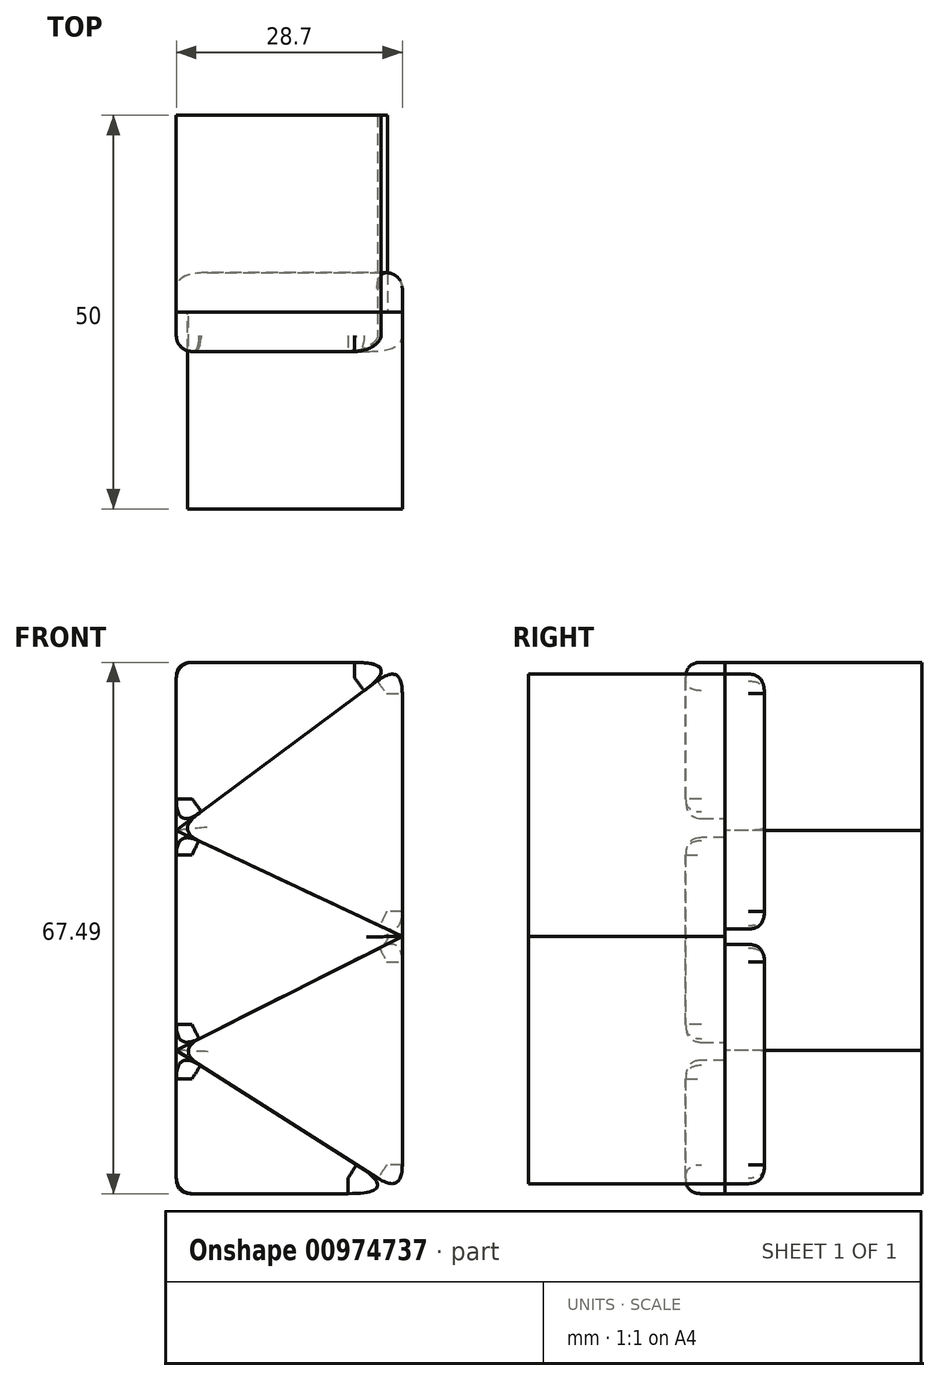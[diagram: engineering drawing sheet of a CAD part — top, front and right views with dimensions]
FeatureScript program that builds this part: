
annotation { "Feature Type Name" : "Feature", "Feature Type Description" : "" }
export const myFeature = defineFeature(function(context is Context, id is Id, definition is map)
    precondition{}
    {
        {
            var Q0;
            Q0=qCreatedBy(makeId("Front.planeOp"),FACE);
            var sketch = newSketch(context, id + "F0", { "sketchPlane" : qUnion([Q0])});
            skLineSegment(sketch, "E0.bottom", {"start": v(-14.25, 34.81) * mm, "end": v(14.45, 34.81) * mm});
            skLineSegment(sketch, "E0.top", {"start": v(-14.25, -32.68) * mm, "end": v(14.45, -32.68) * mm});
            skLineSegment(sketch, "E0.left", {"start": v(-14.25, 34.81) * mm, "end": v(-14.25, -32.68) * mm});
            skLineSegment(sketch, "E0.right", {"start": v(14.45, 34.81) * mm, "end": v(14.45, -32.68) * mm});
            skLineSegment(sketch, "E1", {"start": v(-14.25, 13.48) * mm, "end": v(14.45, 34.81) * mm});
            skLineSegment(sketch, "E2", {"start": v(-14.25, 13.48) * mm, "end": v(14.45, 0) * mm});
            skLineSegment(sketch, "E3", {"start": v(14.45, 0) * mm, "end": v(-14.25, -14.45) * mm});
            skLineSegment(sketch, "E4", {"start": v(-14.25, -14.45) * mm, "end": v(14.45, -32.68) * mm});
            skSolve(sketch);
        }
        {
            var Q0;
            {var subQ0=sQuery(id+"F0.wireOp",EDGE,"E1");Q0=makeQuery(id+"F0.imprint","IMPRINT",FACE,{"disambiguationData":[TD([[makeQuery(id+"F0.imprint","IMPRINT",EDGE,{"derivedFrom":subQ0}),-1.0]])]});}
            var Q1;
            {var subQ2=sQuery(id+"F0.wireOp",EDGE,"E3");Q1=makeQuery(id+"F0.imprint","IMPRINT",FACE,{"disambiguationData":[TD([[makeQuery(id+"F0.imprint","IMPRINT",EDGE,{"derivedFrom":subQ2}),1.0]])]});}
            extrude(context, id + "F1", {"entities" : qUnion([Q0, Q1]), "depth" : 25 * mm, "offsetDistance" : 25 * mm});
        }
        {
            var Q0;
            {var subQ0=sQuery(id+"F0.wireOp",EDGE,"E2");Q0=makeQuery(id+"F0.imprint","IMPRINT",FACE,{"disambiguationData":[TD([[makeQuery(id+"F0.imprint","IMPRINT",EDGE,{"derivedFrom":subQ0}),-1.0]])]});}
            var Q1;
            {var subQ0=sQuery(id+"F0.wireOp",EDGE,"E0.bottom");Q1=makeQuery(id+"F0.imprint","IMPRINT",FACE,{"disambiguationData":[TD([[makeQuery(id+"F0.imprint","IMPRINT",EDGE,{"derivedFrom":subQ0}),-1.0]])]});}
            var Q2;
            {var subQ0=sQuery(id+"F0.wireOp",EDGE,"E0.top");Q2=makeQuery(id+"F0.imprint","IMPRINT",FACE,{"disambiguationData":[TD([[makeQuery(id+"F0.imprint","IMPRINT",EDGE,{"derivedFrom":subQ0}),1.0]])]});}
            extrude(context, id + "F2", {"entities" : qUnion([Q0, Q1, Q2]), "oppositeDirection" : true, "depth" : 25 * mm, "offsetDistance" : 25 * mm});
        }
        {
            var Q0;
            {var subQ0=sQuery(id+"F0.wireOp",EDGE,"E1");Q0=makeQuery(id+"F0.imprint","IMPRINT",FACE,{"disambiguationData":[TD([[makeQuery(id+"F0.imprint","IMPRINT",EDGE,{"derivedFrom":subQ0}),-1.0]])]});}
            var Q1;
            {var subQ2=sQuery(id+"F0.wireOp",EDGE,"E3");Q1=makeQuery(id+"F0.imprint","IMPRINT",FACE,{"disambiguationData":[TD([[makeQuery(id+"F0.imprint","IMPRINT",EDGE,{"derivedFrom":subQ2}),1.0]])]});}
            extrude(context, id + "F3", {"entities" : qUnion([Q0, Q1]), "oppositeDirection" : true, "depth" : 5 * mm, "offsetDistance" : 25 * mm});
        }
        {
            var Q0;
            {var subQ0=sQuery(id+"F0.wireOp",EDGE,"E0.bottom");Q0=makeQuery(id+"F0.imprint","IMPRINT",FACE,{"disambiguationData":[TD([[makeQuery(id+"F0.imprint","IMPRINT",EDGE,{"derivedFrom":subQ0}),-1.0]])]});}
            var Q1;
            {var subQ0=sQuery(id+"F0.wireOp",EDGE,"E2");Q1=makeQuery(id+"F0.imprint","IMPRINT",FACE,{"disambiguationData":[TD([[makeQuery(id+"F0.imprint","IMPRINT",EDGE,{"derivedFrom":subQ0}),-1.0]])]});}
            var Q2;
            {var subQ0=sQuery(id+"F0.wireOp",EDGE,"E0.top");Q2=makeQuery(id+"F0.imprint","IMPRINT",FACE,{"disambiguationData":[TD([[makeQuery(id+"F0.imprint","IMPRINT",EDGE,{"derivedFrom":subQ0}),1.0]])]});}
            extrude(context, id + "F4", {"entities" : qUnion([Q0, Q1, Q2]), "depth" : 5 * mm, "offsetDistance" : 25 * mm});
        }
        {
            var Q0;
            {var subQ0=sQuery(id+"F0.wireOp",EDGE,"E0.left");Q0=makeQuery(id+"F4.opExtrude","CAP_EDGE",EDGE,{"disambiguationData":[OSD([subQ0]),TDD([makeQuery(id+"F0.imprint","IMPRINT",EDGE,{"disambiguationData":[TD([[makeQuery(id+"F0.imprint","INTERSECT",VERTEX,{"derivedFrom":[sQuery(id+"F0.wireOp",EDGE,"E0.bottom"),subQ0]}),-1.0]])],"derivedFrom":subQ0})])],"isStart":false});}
            var Q1;
            {var subQ0=sQuery(id+"F0.wireOp",EDGE,"E0.left");Q1=makeQuery(id+"F4.opExtrude","CAP_EDGE",EDGE,{"disambiguationData":[OSD([subQ0]),TDD([makeQuery(id+"F0.imprint","IMPRINT",EDGE,{"disambiguationData":[TD([[makeQuery(id+"F0.imprint","INTERSECT",VERTEX,{"derivedFrom":[subQ0,sQuery(id+"F0.wireOp",EDGE,"E1"),sQuery(id+"F0.wireOp",EDGE,"E2")]}),-1.0]])],"derivedFrom":subQ0})])],"isStart":false});}
            var Q2;
            {var subQ0=sQuery(id+"F0.wireOp",EDGE,"E0.left");Q2=makeQuery(id+"F4.opExtrude","CAP_EDGE",EDGE,{"disambiguationData":[OSD([subQ0]),TDD([makeQuery(id+"F0.imprint","IMPRINT",EDGE,{"disambiguationData":[TD([[makeQuery(id+"F0.imprint","INTERSECT",VERTEX,{"derivedFrom":[sQuery(id+"F0.wireOp",EDGE,"E0.top"),subQ0]}),1.0]])],"derivedFrom":subQ0})])],"isStart":false});}
            var Q3;
            {var subQ0=sQuery(id+"F0.wireOp",EDGE,"E0.right");Q3=makeQuery(id+"F3.opExtrude","CAP_EDGE",EDGE,{"disambiguationData":[OSD([subQ0]),TDD([makeQuery(id+"F0.imprint","IMPRINT",EDGE,{"disambiguationData":[TD([[makeQuery(id+"F0.imprint","INTERSECT",VERTEX,{"derivedFrom":[sQuery(id+"F0.wireOp",EDGE,"E0.bottom"),subQ0,sQuery(id+"F0.wireOp",EDGE,"E1")]}),-1.0]])],"derivedFrom":subQ0})])],"isStart":false});}
            var Q4;
            {var subQ0=sQuery(id+"F0.wireOp",EDGE,"E0.right");Q4=makeQuery(id+"F3.opExtrude","CAP_EDGE",EDGE,{"disambiguationData":[OSD([subQ0]),TDD([makeQuery(id+"F0.imprint","IMPRINT",EDGE,{"disambiguationData":[TD([[makeQuery(id+"F0.imprint","INTERSECT",VERTEX,{"derivedFrom":[sQuery(id+"F0.wireOp",EDGE,"E0.top"),subQ0,sQuery(id+"F0.wireOp",EDGE,"E4")]}),1.0]])],"derivedFrom":subQ0})])],"isStart":false});}
            fillet(context, id + "F5", {"entities" : qUnion([Q0, Q1, Q2, Q3, Q4]), "radius" : 2 * mm, "tangentPropagation" : true, "allowEdgeOverflow" : false});
        }
        {
            var Q0;
            Q0=makeQuery(id+"F2.opExtrude","SWEPT_EDGE",EDGE,{"disambiguationData":[OSD([sQuery(id+"F0.wireOp",EDGE,"E0.bottom"),sQuery(id+"F0.wireOp",EDGE,"E0.right"),sQuery(id+"F0.wireOp",EDGE,"E1")])]});
            var Q1;
            Q1=makeQuery(id+"F2.opExtrude","SWEPT_EDGE",EDGE,{"disambiguationData":[OSD([sQuery(id+"F0.wireOp",EDGE,"E0.right"),sQuery(id+"F0.wireOp",EDGE,"E2"),sQuery(id+"F0.wireOp",EDGE,"E3")])]});
            var Q2;
            Q2=makeQuery(id+"F2.opExtrude","SWEPT_EDGE",EDGE,{"disambiguationData":[OSD([sQuery(id+"F0.wireOp",EDGE,"E0.top"),sQuery(id+"F0.wireOp",EDGE,"E0.right"),sQuery(id+"F0.wireOp",EDGE,"E4")])]});
            fillet(context, id + "F6", {"entities" : qUnion([Q0, Q1, Q2]), "radius" : 2 * mm, "tangentPropagation" : true, "rho" : 0.5, "crossSection" : FilletCrossSection.CONIC, "allowEdgeOverflow" : false});
        }
        {
            var Q0;
            Q0=makeQuery(id+"F1.opExtrude","SWEPT_EDGE",EDGE,{"disambiguationData":[OSD([sQuery(id+"F0.wireOp",EDGE,"E0.left"),sQuery(id+"F0.wireOp",EDGE,"E1"),sQuery(id+"F0.wireOp",EDGE,"E2")])]});
            var Q1;
            Q1=makeQuery(id+"F1.opExtrude","SWEPT_EDGE",EDGE,{"disambiguationData":[OSD([sQuery(id+"F0.wireOp",EDGE,"E0.left"),sQuery(id+"F0.wireOp",EDGE,"E3"),sQuery(id+"F0.wireOp",EDGE,"E4")])]});
            fillet(context, id + "F7", {"entities" : qUnion([Q0, Q1]), "radius" : 2 * mm, "tangentPropagation" : true, "rho" : 0.5, "crossSection" : FilletCrossSection.CONIC, "allowEdgeOverflow" : false});
        }
        {
            var Q0;
            {var subQ0=sQuery(id+"F0.wireOp",EDGE,"E1");var subQ1=sQuery(id+"F0.wireOp",EDGE,"E0.right");Q0=makeQuery(id+"F5.opFillet","BLEND_EDGE",EDGE,{"blendedFrom":[makeQuery(id+"F3.opExtrude","CAP_EDGE",EDGE,{"disambiguationData":[OSD([subQ1]),TDD([makeQuery(id+"F0.imprint","IMPRINT",EDGE,{"disambiguationData":[TD([[makeQuery(id+"F0.imprint","INTERSECT",VERTEX,{"derivedFrom":[sQuery(id+"F0.wireOp",EDGE,"E0.bottom"),subQ1,subQ0]}),-1.0]])],"derivedFrom":subQ1})])],"isStart":false}),makeQuery(id+"F3.opExtrude","SWEPT_FACE",FACE,{"disambiguationData":[OSD([subQ0])]})],"blendedInto":[makeQuery(id+"F3.opExtrude","SWEPT_FACE",FACE,{"disambiguationData":[OSD([subQ0])]})]});}
            var Q1;
            {var subQ0=sQuery(id+"F0.wireOp",EDGE,"E4");var subQ1=sQuery(id+"F0.wireOp",EDGE,"E0.right");Q1=makeQuery(id+"F5.opFillet","BLEND_EDGE",EDGE,{"blendedFrom":[makeQuery(id+"F3.opExtrude","CAP_EDGE",EDGE,{"disambiguationData":[OSD([subQ1]),TDD([makeQuery(id+"F0.imprint","IMPRINT",EDGE,{"disambiguationData":[TD([[makeQuery(id+"F0.imprint","INTERSECT",VERTEX,{"derivedFrom":[sQuery(id+"F0.wireOp",EDGE,"E0.top"),subQ1,subQ0]}),1.0]])],"derivedFrom":subQ1})])],"isStart":false}),makeQuery(id+"F3.opExtrude","SWEPT_FACE",FACE,{"disambiguationData":[OSD([subQ0])]})],"blendedInto":[makeQuery(id+"F3.opExtrude","SWEPT_FACE",FACE,{"disambiguationData":[OSD([subQ0])]})]});}
            var Q2;
            {var subQ0=sQuery(id+"F0.wireOp",EDGE,"E2");var subQ1=sQuery(id+"F0.wireOp",EDGE,"E0.left");Q2=makeQuery(id+"F5.opFillet","BLEND_EDGE",EDGE,{"blendedFrom":[makeQuery(id+"F4.opExtrude","CAP_EDGE",EDGE,{"disambiguationData":[OSD([subQ1]),TDD([makeQuery(id+"F0.imprint","IMPRINT",EDGE,{"disambiguationData":[TD([[makeQuery(id+"F0.imprint","INTERSECT",VERTEX,{"derivedFrom":[subQ1,sQuery(id+"F0.wireOp",EDGE,"E1"),subQ0]}),-1.0]])],"derivedFrom":subQ1})])],"isStart":false}),makeQuery(id+"F4.opExtrude","SWEPT_FACE",FACE,{"disambiguationData":[OSD([subQ0])]})],"blendedInto":[makeQuery(id+"F4.opExtrude","SWEPT_FACE",FACE,{"disambiguationData":[OSD([subQ0])]})]});}
            var Q3;
            {var subQ0=sQuery(id+"F0.wireOp",EDGE,"E1");var subQ1=sQuery(id+"F0.wireOp",EDGE,"E0.left");Q3=makeQuery(id+"F5.opFillet","BLEND_EDGE",EDGE,{"blendedFrom":[makeQuery(id+"F4.opExtrude","CAP_EDGE",EDGE,{"disambiguationData":[OSD([subQ1]),TDD([makeQuery(id+"F0.imprint","IMPRINT",EDGE,{"disambiguationData":[TD([[makeQuery(id+"F0.imprint","INTERSECT",VERTEX,{"derivedFrom":[sQuery(id+"F0.wireOp",EDGE,"E0.bottom"),subQ1]}),-1.0]])],"derivedFrom":subQ1})])],"isStart":false}),makeQuery(id+"F4.opExtrude","SWEPT_FACE",FACE,{"disambiguationData":[OSD([subQ0])]})],"blendedInto":[makeQuery(id+"F4.opExtrude","SWEPT_FACE",FACE,{"disambiguationData":[OSD([subQ0])]})]});}
            var Q4;
            {var subQ0=sQuery(id+"F0.wireOp",EDGE,"E3");var subQ1=sQuery(id+"F0.wireOp",EDGE,"E0.left");Q4=makeQuery(id+"F5.opFillet","BLEND_EDGE",EDGE,{"blendedFrom":[makeQuery(id+"F4.opExtrude","CAP_EDGE",EDGE,{"disambiguationData":[OSD([subQ1]),TDD([makeQuery(id+"F0.imprint","IMPRINT",EDGE,{"disambiguationData":[TD([[makeQuery(id+"F0.imprint","INTERSECT",VERTEX,{"derivedFrom":[subQ1,sQuery(id+"F0.wireOp",EDGE,"E1"),sQuery(id+"F0.wireOp",EDGE,"E2")]}),-1.0]])],"derivedFrom":subQ1})])],"isStart":false}),makeQuery(id+"F4.opExtrude","SWEPT_FACE",FACE,{"disambiguationData":[OSD([subQ0])]})],"blendedInto":[makeQuery(id+"F4.opExtrude","SWEPT_FACE",FACE,{"disambiguationData":[OSD([subQ0])]})]});}
            var Q5;
            {var subQ0=sQuery(id+"F0.wireOp",EDGE,"E4");var subQ1=sQuery(id+"F0.wireOp",EDGE,"E0.left");Q5=makeQuery(id+"F5.opFillet","BLEND_EDGE",EDGE,{"blendedFrom":[makeQuery(id+"F4.opExtrude","CAP_EDGE",EDGE,{"disambiguationData":[OSD([subQ1]),TDD([makeQuery(id+"F0.imprint","IMPRINT",EDGE,{"disambiguationData":[TD([[makeQuery(id+"F0.imprint","INTERSECT",VERTEX,{"derivedFrom":[sQuery(id+"F0.wireOp",EDGE,"E0.top"),subQ1]}),1.0]])],"derivedFrom":subQ1})])],"isStart":false}),makeQuery(id+"F4.opExtrude","SWEPT_FACE",FACE,{"disambiguationData":[OSD([subQ0])]})],"blendedInto":[makeQuery(id+"F4.opExtrude","SWEPT_FACE",FACE,{"disambiguationData":[OSD([subQ0])]})]});}
            var Q6;
            {var subQ0=sQuery(id+"F0.wireOp",EDGE,"E3");var subQ1=sQuery(id+"F0.wireOp",EDGE,"E0.right");Q6=makeQuery(id+"F5.opFillet","BLEND_EDGE",EDGE,{"blendedFrom":[makeQuery(id+"F3.opExtrude","CAP_EDGE",EDGE,{"disambiguationData":[OSD([subQ1]),TDD([makeQuery(id+"F0.imprint","IMPRINT",EDGE,{"disambiguationData":[TD([[makeQuery(id+"F0.imprint","INTERSECT",VERTEX,{"derivedFrom":[sQuery(id+"F0.wireOp",EDGE,"E0.top"),subQ1,sQuery(id+"F0.wireOp",EDGE,"E4")]}),1.0]])],"derivedFrom":subQ1})])],"isStart":false}),makeQuery(id+"F3.opExtrude","SWEPT_FACE",FACE,{"disambiguationData":[OSD([subQ0])]})],"blendedInto":[makeQuery(id+"F3.opExtrude","SWEPT_FACE",FACE,{"disambiguationData":[OSD([subQ0])]})]});}
            var Q7;
            {var subQ0=sQuery(id+"F0.wireOp",EDGE,"E2");var subQ1=sQuery(id+"F0.wireOp",EDGE,"E0.right");Q7=makeQuery(id+"F5.opFillet","BLEND_EDGE",EDGE,{"blendedFrom":[makeQuery(id+"F3.opExtrude","CAP_EDGE",EDGE,{"disambiguationData":[OSD([subQ1]),TDD([makeQuery(id+"F0.imprint","IMPRINT",EDGE,{"disambiguationData":[TD([[makeQuery(id+"F0.imprint","INTERSECT",VERTEX,{"derivedFrom":[sQuery(id+"F0.wireOp",EDGE,"E0.bottom"),subQ1,sQuery(id+"F0.wireOp",EDGE,"E1")]}),-1.0]])],"derivedFrom":subQ1})])],"isStart":false}),makeQuery(id+"F3.opExtrude","SWEPT_FACE",FACE,{"disambiguationData":[OSD([subQ0])]})],"blendedInto":[makeQuery(id+"F3.opExtrude","SWEPT_FACE",FACE,{"disambiguationData":[OSD([subQ0])]})]});}
            fillet(context, id + "F8", {"entities" : qUnion([Q0, Q1, Q2, Q3, Q4, Q5, Q6, Q7]), "radius" : 2 * mm, "tangentPropagation" : true, "rho" : 0.5, "crossSection" : FilletCrossSection.CONIC, "allowEdgeOverflow" : false});
        }
        {
            var Q0;
            Q0=makeQuery(id+"F8.opFillet","BLEND_EDGE",EDGE,{"blendedFrom":[makeQuery(id+"F4.opExtrude","CAP_EDGE",EDGE,{"disambiguationData":[OSD([sQuery(id+"F0.wireOp",EDGE,"E1")])],"isStart":false}),makeQuery(id+"F4.opExtrude","SWEPT_FACE",FACE,{"disambiguationData":[OSD([sQuery(id+"F0.wireOp",EDGE,"E0.bottom")])]})],"blendedInto":[makeQuery(id+"F4.opExtrude","SWEPT_FACE",FACE,{"disambiguationData":[OSD([sQuery(id+"F0.wireOp",EDGE,"E0.bottom")])]})]});
            var Q1;
            Q1=makeQuery(id+"F8.opFillet","BLEND_EDGE",EDGE,{"blendedFrom":[makeQuery(id+"F4.opExtrude","CAP_EDGE",EDGE,{"disambiguationData":[OSD([sQuery(id+"F0.wireOp",EDGE,"E4")])],"isStart":false}),makeQuery(id+"F4.opExtrude","SWEPT_FACE",FACE,{"disambiguationData":[OSD([sQuery(id+"F0.wireOp",EDGE,"E0.top")])]})],"blendedInto":[makeQuery(id+"F4.opExtrude","SWEPT_FACE",FACE,{"disambiguationData":[OSD([sQuery(id+"F0.wireOp",EDGE,"E0.top")])]})]});
            fillet(context, id + "F9", {"entities" : qUnion([Q0, Q1]), "radius" : 2 * mm, "tangentPropagation" : true, "rho" : 0.5, "crossSection" : FilletCrossSection.CONIC, "allowEdgeOverflow" : false});
        }
        {
            var Q0;
            Q0=makeQuery(id+"F2.opExtrude","SWEPT_EDGE",EDGE,{"disambiguationData":[OSD([sQuery(id+"F0.wireOp",EDGE,"E0.bottom"),sQuery(id+"F0.wireOp",EDGE,"E0.left")])]});
            var Q1;
            Q1=makeQuery(id+"F2.opExtrude","SWEPT_EDGE",EDGE,{"disambiguationData":[OSD([sQuery(id+"F0.wireOp",EDGE,"E0.top"),sQuery(id+"F0.wireOp",EDGE,"E0.left")])]});
            fillet(context, id + "F10", {"entities" : qUnion([Q0, Q1]), "radius" : 2 * mm, "tangentPropagation" : true, "allowEdgeOverflow" : false});
        }
        {
            var Q0;
            Q0=makeQuery(id+"F1.opExtrude","SWEPT_EDGE",EDGE,{"disambiguationData":[OSD([sQuery(id+"F0.wireOp",EDGE,"E0.top"),sQuery(id+"F0.wireOp",EDGE,"E0.right"),sQuery(id+"F0.wireOp",EDGE,"E4")])]});
            var Q1;
            Q1=makeQuery(id+"F1.opExtrude","SWEPT_EDGE",EDGE,{"disambiguationData":[OSD([sQuery(id+"F0.wireOp",EDGE,"E0.bottom"),sQuery(id+"F0.wireOp",EDGE,"E0.right"),sQuery(id+"F0.wireOp",EDGE,"E1")])]});
            fillet(context, id + "F11", {"entities" : qUnion([Q0, Q1]), "radius" : 2 * mm, "tangentPropagation" : true, "rho" : 0.5, "crossSection" : FilletCrossSection.CONIC, "allowEdgeOverflow" : false});
        }
    });
